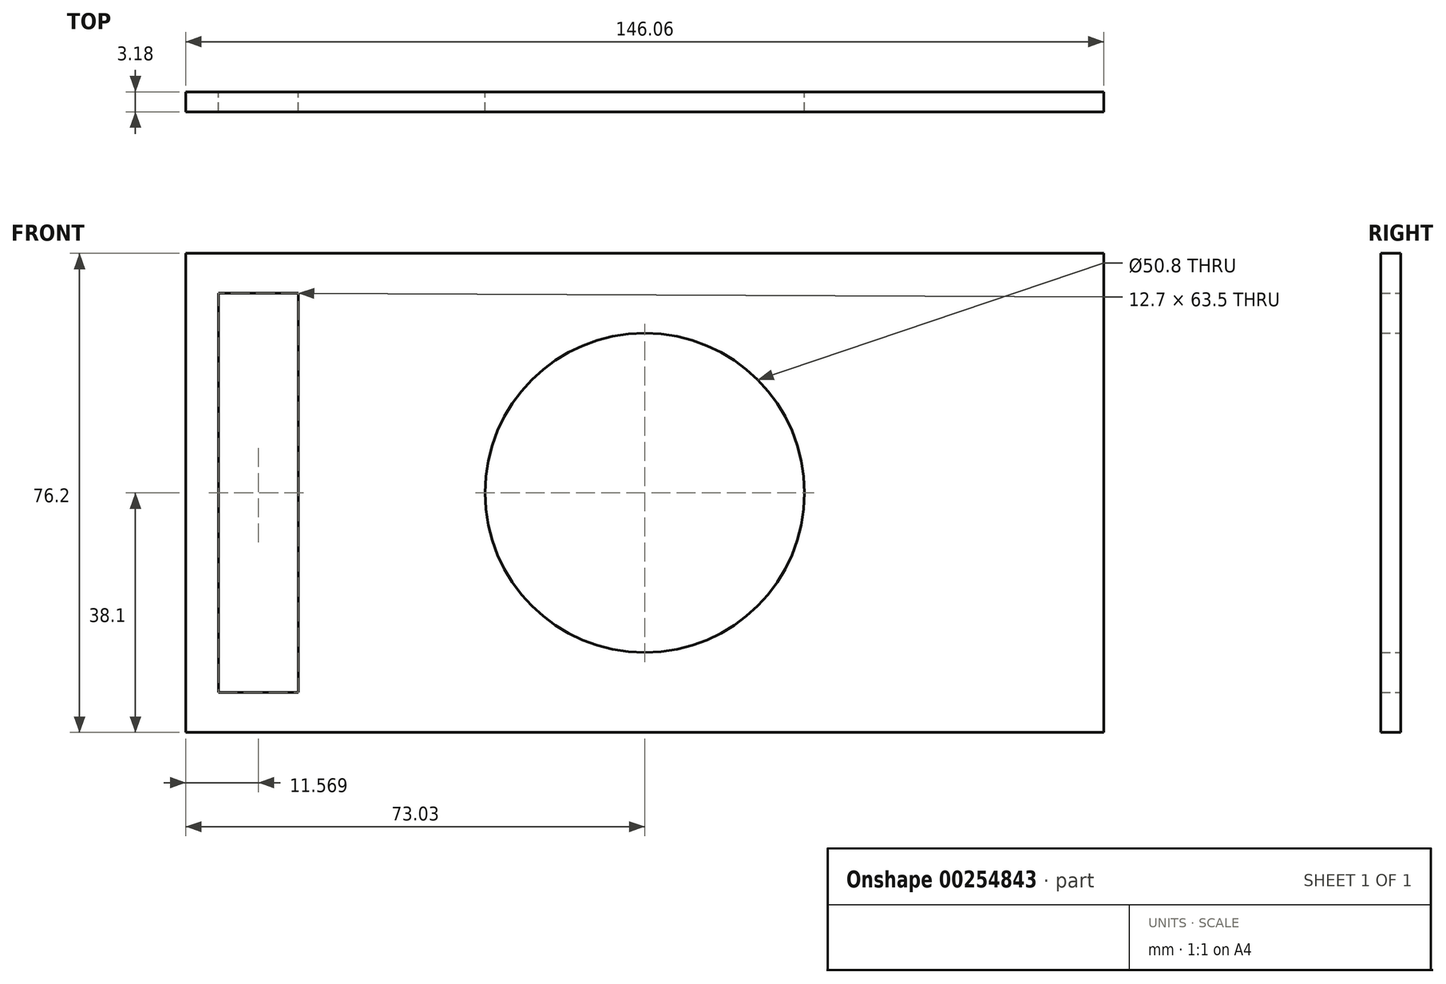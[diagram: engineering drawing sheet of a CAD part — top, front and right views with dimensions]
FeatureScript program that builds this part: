
annotation { "Feature Type Name" : "Feature", "Feature Type Description" : "" }
export const myFeature = defineFeature(function(context is Context, id is Id, definition is map)
    precondition{}
    {
        {
            var Q0;
            Q0=qCreatedBy(makeId("Front.planeOp"),FACE);
            var sketch = newSketch(context, id + "F0", { "sketchPlane" : qUnion([Q0])});
            skLineSegment(sketch, "E0.bottom", {"start": v(-73.02, -38.1) * mm, "end": v(73.03, -38.1) * mm});
            skLineSegment(sketch, "E0.top", {"start": v(-73.03, 38.1) * mm, "end": v(73.02, 38.1) * mm});
            skLineSegment(sketch, "E0.left", {"start": v(-73.02, -38.1) * mm, "end": v(-73.03, 38.1) * mm});
            skLineSegment(sketch, "E0.right", {"start": v(73.03, -38.1) * mm, "end": v(73.02, 38.1) * mm});
            skPoint(sketch, "E0.middle", {"position": v(0, 0) * mm});
            skCircle(sketch, "E1", {"center": v(0, 0) * mm, "radius": 25.4 * mm});
            skLineSegment(sketch, "E2.bottom", {"start": v(-67.81, -31.75) * mm, "end": v(-55.11, -31.75) * mm});
            skLineSegment(sketch, "E2.top", {"start": v(-67.81, 31.75) * mm, "end": v(-55.11, 31.75) * mm});
            skLineSegment(sketch, "E2.left", {"start": v(-67.81, -31.75) * mm, "end": v(-67.81, 31.75) * mm});
            skLineSegment(sketch, "E2.right", {"start": v(-55.11, -31.75) * mm, "end": v(-55.11, 31.75) * mm});
            skPoint(sketch, "E2.middle", {"position": v(-61.46, 0) * mm});
            skSolve(sketch);
        }
        {
            var Q0;
            Q0=makeQuery(id+"F0.imprint","IMPRINT",FACE,{"disambiguationData":[TD([[makeQuery(id+"F0.imprint","IMPRINT",EDGE,{"derivedFrom":sQuery(id+"F0.wireOp",EDGE,"E0.bottom")}),1.0]])]});
            extrude(context, id + "F1", {"entities" : qUnion([Q0]), "endBound" : BoundingType.SYMMETRIC, "depth" : 3.17 * mm});
        }
    });
